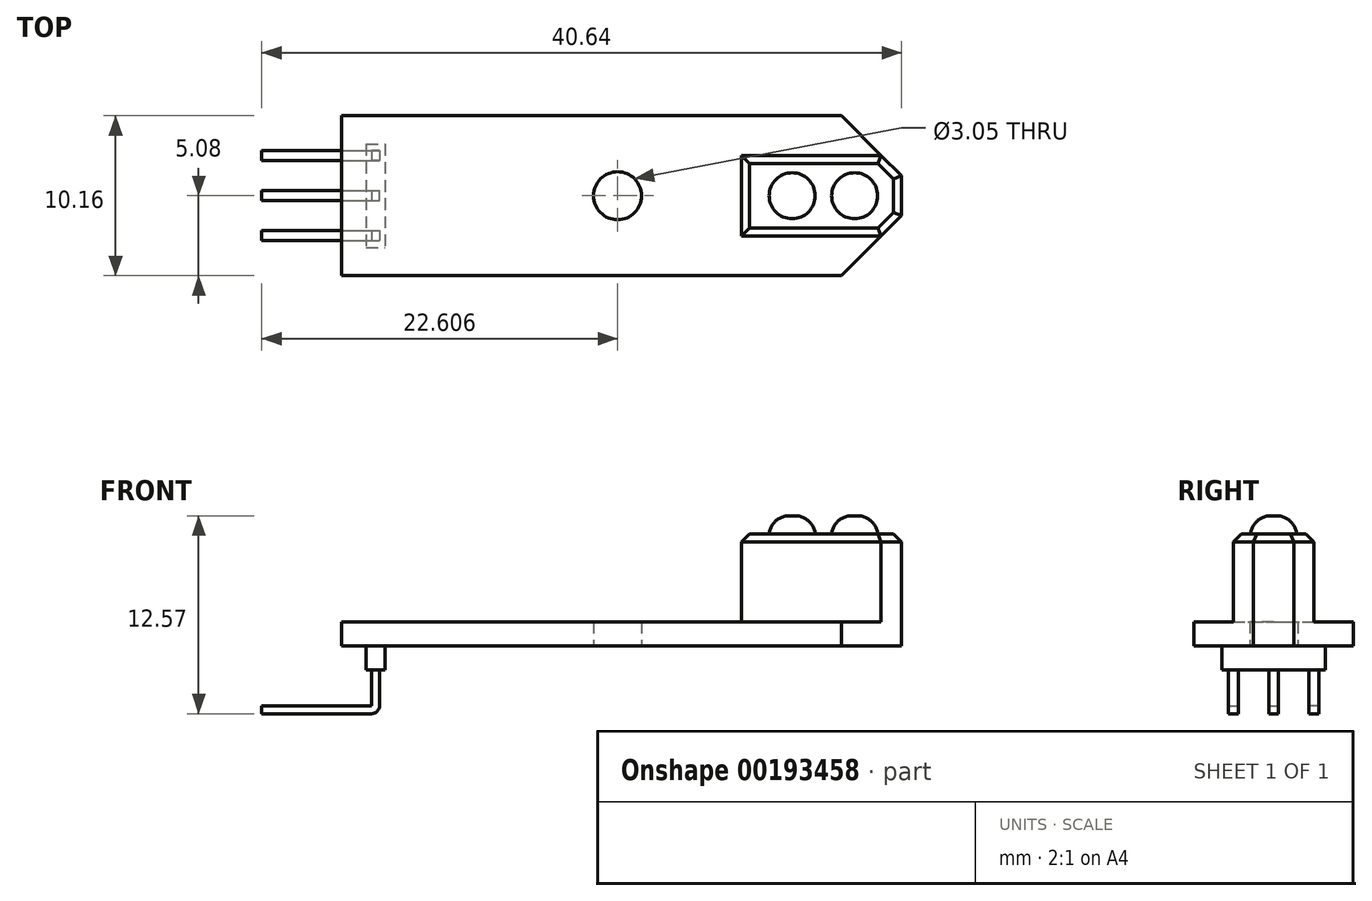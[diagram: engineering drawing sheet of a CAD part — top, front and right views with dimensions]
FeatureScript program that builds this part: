
annotation { "Feature Type Name" : "Feature", "Feature Type Description" : "" }
export const myFeature = defineFeature(function(context is Context, id is Id, definition is map)
    precondition{}
    {
        {
            var Q0;
            Q0=qCreatedBy(makeId("Top.planeOp"),FACE);
            var sketch = newSketch(context, id + "F0", { "sketchPlane" : qUnion([Q0])});
            skLineSegment(sketch, "E0.bottom", {"start": v(13.97, -5.08) * mm, "end": v(-17.78, -5.08) * mm});
            skLineSegment(sketch, "E0.top", {"start": v(13.97, 5.08) * mm, "end": v(-17.78, 5.08) * mm});
            skLineSegment(sketch, "E0.left", {"start": v(17.78, -1.27) * mm, "end": v(17.78, 1.27) * mm});
            skLineSegment(sketch, "E0.right", {"start": v(-17.78, -5.08) * mm, "end": v(-17.78, 5.08) * mm});
            skPoint(sketch, "E0.middle", {"position": v(0, 0) * mm});
            skLineSegment(sketch, "E1", {"start": v(13.97, 5.08) * mm, "end": v(17.78, 1.27) * mm});
            skLineSegment(sketch, "E2", {"start": v(0, 0) * mm, "end": v(10.97, 0) * mm, "construction": true});
            skLineSegment(sketch, "E3.MirrorCS", {"start": v(13.97, -5.08) * mm, "end": v(17.78, -1.27) * mm});
            skPoint(sketch, "E4.orphan", {"position": v(17.78, 5.08) * mm});
            skPoint(sketch, "E5.orphan", {"position": v(17.78, -5.08) * mm});
            skLineSegment(sketch, "E6.bottom", {"start": v(7.62, -2.57) * mm, "end": v(17.78, -2.57) * mm});
            skLineSegment(sketch, "E6.top", {"start": v(7.62, 2.57) * mm, "end": v(17.78, 2.57) * mm});
            skLineSegment(sketch, "E6.left", {"start": v(7.62, -2.57) * mm, "end": v(7.62, 2.57) * mm});
            skLineSegment(sketch, "E6.right", {"start": v(17.78, -2.57) * mm, "end": v(17.78, 2.57) * mm});
            skPoint(sketch, "E6.middle", {"position": v(12.7, 0) * mm});
            skPoint(sketch, "E6.middle.positionSnap0", {"position": v(5.48, 0) * mm});
            skPoint(sketch, "E6.centerSnap0", {"position": v(5.48, 0) * mm});
            skSolve(sketch);
        }
        {
            var Q0;
            {var subQ4=sQuery(id+"F0.wireOp",EDGE,"E0.bottom");Q0=makeQuery(id+"F0.imprint","IMPRINT",FACE,{"disambiguationData":[TD([[makeQuery(id+"F0.imprint","IMPRINT",EDGE,{"derivedFrom":subQ4}),-1.0]])]});}
            var Q1;
            {var subQ0=sQuery(id+"F0.wireOp",EDGE,"E6.left");Q1=makeQuery(id+"F0.imprint","IMPRINT",FACE,{"disambiguationData":[TD([[makeQuery(id+"F0.imprint","IMPRINT",EDGE,{"derivedFrom":subQ0}),-1.0]])]});}
            extrude(context, id + "F1", {"entities" : qUnion([Q0, Q1]), "oppositeDirection" : true, "depth" : 1.52 * mm});
        }
        {
            var Q0;
            {var subQ4=sQuery(id+"F0.wireOp",EDGE,"E0.bottom");Q0=makeQuery(id+"F0.imprint","IMPRINT",FACE,{"disambiguationData":[TD([[makeQuery(id+"F0.imprint","IMPRINT",EDGE,{"derivedFrom":subQ4}),-1.0]])]});}
            var sketch = newSketch(context, id + "F2", { "sketchPlane" : qUnion([Q0])});
            skLineSegment(sketch, "E7.0", {"start": v(17.78, -1.27) * mm, "end": v(17.78, 1.27) * mm});
            skLineSegment(sketch, "E8.0", {"start": v(7.62, 2.57) * mm, "end": v(16.48, 2.57) * mm});
            skLineSegment(sketch, "E9.0", {"start": v(7.62, -2.57) * mm, "end": v(16.48, -2.57) * mm});
            skLineSegment(sketch, "E10.0", {"start": v(7.62, -2.57) * mm, "end": v(7.62, 2.57) * mm});
            skLineSegment(sketch, "E11.0", {"start": v(16.48, -2.57) * mm, "end": v(17.78, -1.27) * mm});
            skLineSegment(sketch, "E12.0", {"start": v(16.48, 2.57) * mm, "end": v(17.78, 1.27) * mm});
            skPoint(sketch, "E13.orphan", {"position": v(13.97, 5.08) * mm});
            skPoint(sketch, "E14.orphan", {"position": v(17.78, 2.57) * mm});
            skPoint(sketch, "E15.orphan", {"position": v(17.78, -2.57) * mm});
            skPoint(sketch, "E16.orphan", {"position": v(13.97, -5.08) * mm});
            skSolve(sketch);
        }
        {
            var Q0;
            Q0=makeQuery(id+"F2.imprint","IMPRINT",FACE,{"disambiguationData":[TD([[makeQuery(id+"F2.imprint","IMPRINT",EDGE,{"derivedFrom":sQuery(id+"F2.wireOp",EDGE,"E7.0")}),1.0]])]});
            extrude(context, id + "F3", {"entities" : qUnion([Q0]), "operationType" : NewBodyOperationType.ADD, "depth" : 5.6 * mm});
        }
        {
            var Q0;
            Q0=makeQuery(id+"F3.opExtrude","CAP_FACE",FACE,{"disambiguationData":[OSD([sQuery(id+"F2.wireOp",EDGE,"E7.0"),sQuery(id+"F2.wireOp",EDGE,"E8.0"),sQuery(id+"F2.wireOp",EDGE,"E9.0"),sQuery(id+"F2.wireOp",EDGE,"E10.0"),sQuery(id+"F2.wireOp",EDGE,"E11.0"),sQuery(id+"F2.wireOp",EDGE,"E12.0")])],"isStart":false});
            var sketch = newSketch(context, id + "F4", { "sketchPlane" : qUnion([Q0])});
            skCircle(sketch, "E17", {"center": v(14.8, 0) * mm, "radius": 1.46 * mm});
            skCircle(sketch, "E18", {"center": v(10.83, 0) * mm, "radius": 1.46 * mm});
            skPoint(sketch, "E18.centerSnap0", {"position": v(7.62, 0) * mm});
            skSolve(sketch);
        }
        {
            var Q0;
            Q0=makeQuery(id+"F4.imprint","IMPRINT",FACE,{"disambiguationData":[TD([[makeQuery(id+"F4.imprint","IMPRINT",EDGE,{"derivedFrom":sQuery(id+"F4.wireOp",EDGE,"E18")}),1.0]])]});
            var Q1;
            Q1=makeQuery(id+"F4.imprint","IMPRINT",FACE,{"disambiguationData":[TD([[makeQuery(id+"F4.imprint","IMPRINT",EDGE,{"derivedFrom":sQuery(id+"F4.wireOp",EDGE,"E17")}),1.0]])]});
            extrude(context, id + "F5", {"entities" : qUnion([Q0, Q1]), "operationType" : NewBodyOperationType.ADD, "depth" : 1.14 * mm});
        }
        {
            var Q0;
            Q0=makeQuery(id+"F5.opExtrude","CAP_EDGE",EDGE,{"disambiguationData":[OSD([sQuery(id+"F4.wireOp",EDGE,"E18")])],"isStart":false});
            var Q1;
            Q1=makeQuery(id+"F5.opExtrude","CAP_EDGE",EDGE,{"disambiguationData":[OSD([sQuery(id+"F4.wireOp",EDGE,"E17")])],"isStart":false});
            fillet(context, id + "F6", {"entities" : qUnion([Q0, Q1]), "radius" : 1.27 * mm, "tangentPropagation" : true, "allowEdgeOverflow" : false});
        }
        {
            var Q0;
            Q0=makeQuery(id+"F3.opExtrude","CAP_EDGE",EDGE,{"disambiguationData":[OSD([sQuery(id+"F2.wireOp",EDGE,"E9.0")])],"isStart":false});
            var Q1;
            Q1=makeQuery(id+"F3.opExtrude","CAP_EDGE",EDGE,{"disambiguationData":[OSD([sQuery(id+"F2.wireOp",EDGE,"E8.0")])],"isStart":false});
            var Q2;
            Q2=makeQuery(id+"F3.opExtrude","CAP_EDGE",EDGE,{"disambiguationData":[OSD([sQuery(id+"F2.wireOp",EDGE,"E10.0")])],"isStart":false});
            var Q3;
            Q3=makeQuery(id+"F3.opExtrude","CAP_EDGE",EDGE,{"disambiguationData":[OSD([sQuery(id+"F2.wireOp",EDGE,"E7.0")])],"isStart":false});
            var Q4;
            Q4=makeQuery(id+"F3.opExtrude","CAP_EDGE",EDGE,{"disambiguationData":[OSD([sQuery(id+"F2.wireOp",EDGE,"E11.0")])],"isStart":false});
            var Q5;
            Q5=makeQuery(id+"F3.opExtrude","CAP_EDGE",EDGE,{"disambiguationData":[OSD([sQuery(id+"F2.wireOp",EDGE,"E12.0")])],"isStart":false});
            chamfer(context, id + "F7", {"entities" : qUnion([Q0, Q1, Q2, Q3, Q4, Q5]), "width" : 0.5 * mm, "tangentPropagation" : true});
        }
        {
            var Q0;
            Q0=qCreatedBy(makeId("Front.planeOp"),FACE);
            var sketch = newSketch(context, id + "F8", { "sketchPlane" : qUnion([Q0])});
            skLineSegment(sketch, "E19", {"start": v(-22.86, -5.84) * mm, "end": v(-15.92, -5.84) * mm});
            skLineSegment(sketch, "E20", {"start": v(-15.36, -5.29) * mm, "end": v(-15.36, -1.17) * mm});
            skPoint(sketch, "E21.visualSharp", {"position": v(-15.36, -5.84) * mm});
            skArc(sketch, "E21.filletArc", {"start": v(-15.92, -5.84) * mm, "mid": v(-15.52, -5.68) * mm, "end": v(-15.36, -5.29) * mm});
            skLineSegment(sketch, "E22.0", {"start": v(-22.86, -5.33) * mm, "end": v(-15.87, -5.33) * mm});
            skLineSegment(sketch, "E23.0", {"start": v(-15.87, -5.33) * mm, "end": v(-15.87, -1.17) * mm});
            skLineSegment(sketch, "E24", {"start": v(-15.87, -1.17) * mm, "end": v(-15.36, -1.17) * mm});
            skLineSegment(sketch, "E25", {"start": v(-22.86, -5.84) * mm, "end": v(-22.86, -5.33) * mm});
            skSolve(sketch);
        }
        {
            var Q0;
            Q0=makeQuery(id+"F8.imprint","IMPRINT",FACE,{"disambiguationData":[TD([[makeQuery(id+"F8.imprint","IMPRINT",EDGE,{"derivedFrom":sQuery(id+"F8.wireOp",EDGE,"E19")}),1.0]])]});
            extrude(context, id + "F9", {"entities" : qUnion([Q0]), "depth" : 0.64 * mm, "symmetric" : true});
        }
        {
            var Q0;
            Q0=makeQuery(id+"F9.opExtrude","SWEPT_BODY",BODY,{"disambiguationData":[OSD([sQuery(id+"F8.wireOp",EDGE,"E19"),sQuery(id+"F8.wireOp",EDGE,"E20"),sQuery(id+"F8.wireOp",EDGE,"E21.filletArc"),sQuery(id+"F8.wireOp",EDGE,"E22.0"),sQuery(id+"F8.wireOp",EDGE,"E23.0"),sQuery(id+"F8.wireOp",EDGE,"E24"),sQuery(id+"F8.wireOp",EDGE,"E25")])]});
            transform(context, id + "F10", {"entities" : qUnion([Q0]), "transformType" : TransformType.TRANSLATION_3D, "dx" : 0 * mm, "dy" : -2.54 * mm, "dz" : 0 * mm, "makeCopy" : true});
        }
        {
            var Q0;
            Q0=makeQuery(id+"F10.opPattern","COPY",BODY,{"derivedFrom":makeQuery(id+"F9.opExtrude","SWEPT_BODY",BODY,{"disambiguationData":[OSD([sQuery(id+"F8.wireOp",EDGE,"E19"),sQuery(id+"F8.wireOp",EDGE,"E20"),sQuery(id+"F8.wireOp",EDGE,"E21.filletArc"),sQuery(id+"F8.wireOp",EDGE,"E22.0"),sQuery(id+"F8.wireOp",EDGE,"E23.0"),sQuery(id+"F8.wireOp",EDGE,"E24"),sQuery(id+"F8.wireOp",EDGE,"E25")])]}),"instanceName":"1"});
            var Q1;
            Q1=qCreatedBy(makeId("Front.planeOp"),FACE);
            mirror(context, id + "F11", {"operationType" : NewBodyOperationType.ADD, "entities" : qUnion([Q0]), "mirrorPlane" : qUnion([Q1])});
        }
        {
            var Q0;
            Q0=makeQuery(id+"F1.opExtrude","CAP_FACE",FACE,{"disambiguationData":[OSD([sQuery(id+"F0.wireOp",EDGE,"E0.bottom"),sQuery(id+"F0.wireOp",EDGE,"E0.top"),sQuery(id+"F0.wireOp",EDGE,"E0.right"),sQuery(id+"F0.wireOp",EDGE,"E1"),sQuery(id+"F0.wireOp",EDGE,"E3.MirrorCS"),sQuery(id+"F0.wireOp",EDGE,"E6.right")])],"isStart":false});
            var sketch = newSketch(context, id + "F12", { "sketchPlane" : qUnion([Q0])});
            skLineSegment(sketch, "E26.bottom", {"start": v(-16.22, -3.3) * mm, "end": v(-15.02, -3.3) * mm});
            skLineSegment(sketch, "E26.top", {"start": v(-16.22, 3.3) * mm, "end": v(-15.02, 3.3) * mm});
            skLineSegment(sketch, "E26.left", {"start": v(-16.22, -3.3) * mm, "end": v(-16.22, 3.3) * mm});
            skLineSegment(sketch, "E26.right", {"start": v(-15.02, -3.3) * mm, "end": v(-15.02, 3.3) * mm});
            skPoint(sketch, "E26.middle", {"position": v(-15.62, 0) * mm});
            skSolve(sketch);
        }
        {
            var Q0;
            Q0=makeQuery(id+"F12.imprint","IMPRINT",FACE,{"disambiguationData":[TD([[makeQuery(id+"F12.imprint","IMPRINT",EDGE,{"derivedFrom":sQuery(id+"F12.wireOp",EDGE,"E26.bottom")}),1.0]])]});
            extrude(context, id + "F13", {"entities" : qUnion([Q0]), "operationType" : NewBodyOperationType.ADD, "depth" : 1.52 * mm});
        }
        {
            var Q0;
            Q0=makeQuery(id+"F1.opExtrude","CAP_FACE",FACE,{"disambiguationData":[OSD([sQuery(id+"F0.wireOp",EDGE,"E0.bottom"),sQuery(id+"F0.wireOp",EDGE,"E0.top"),sQuery(id+"F0.wireOp",EDGE,"E0.right"),sQuery(id+"F0.wireOp",EDGE,"E1"),sQuery(id+"F0.wireOp",EDGE,"E3.MirrorCS"),sQuery(id+"F0.wireOp",EDGE,"E6.right")])],"isStart":false});
            var sketch = newSketch(context, id + "F14", { "sketchPlane" : qUnion([Q0])});
            skCircle(sketch, "E27", {"center": v(-0.25, 0) * mm, "radius": 1.52 * mm});
            skSolve(sketch);
        }
        {
            var Q0;
            Q0=makeQuery(id+"F14.imprint","IMPRINT",FACE,{"disambiguationData":[TD([[makeQuery(id+"F14.imprint","IMPRINT",EDGE,{"derivedFrom":sQuery(id+"F14.wireOp",EDGE,"E27")}),1.0]])]});
            extrude(context, id + "F15", {"entities" : qUnion([Q0]), "operationType" : NewBodyOperationType.REMOVE, "oppositeDirection" : true, "depth" : 25.4 * mm});
        }
    });
